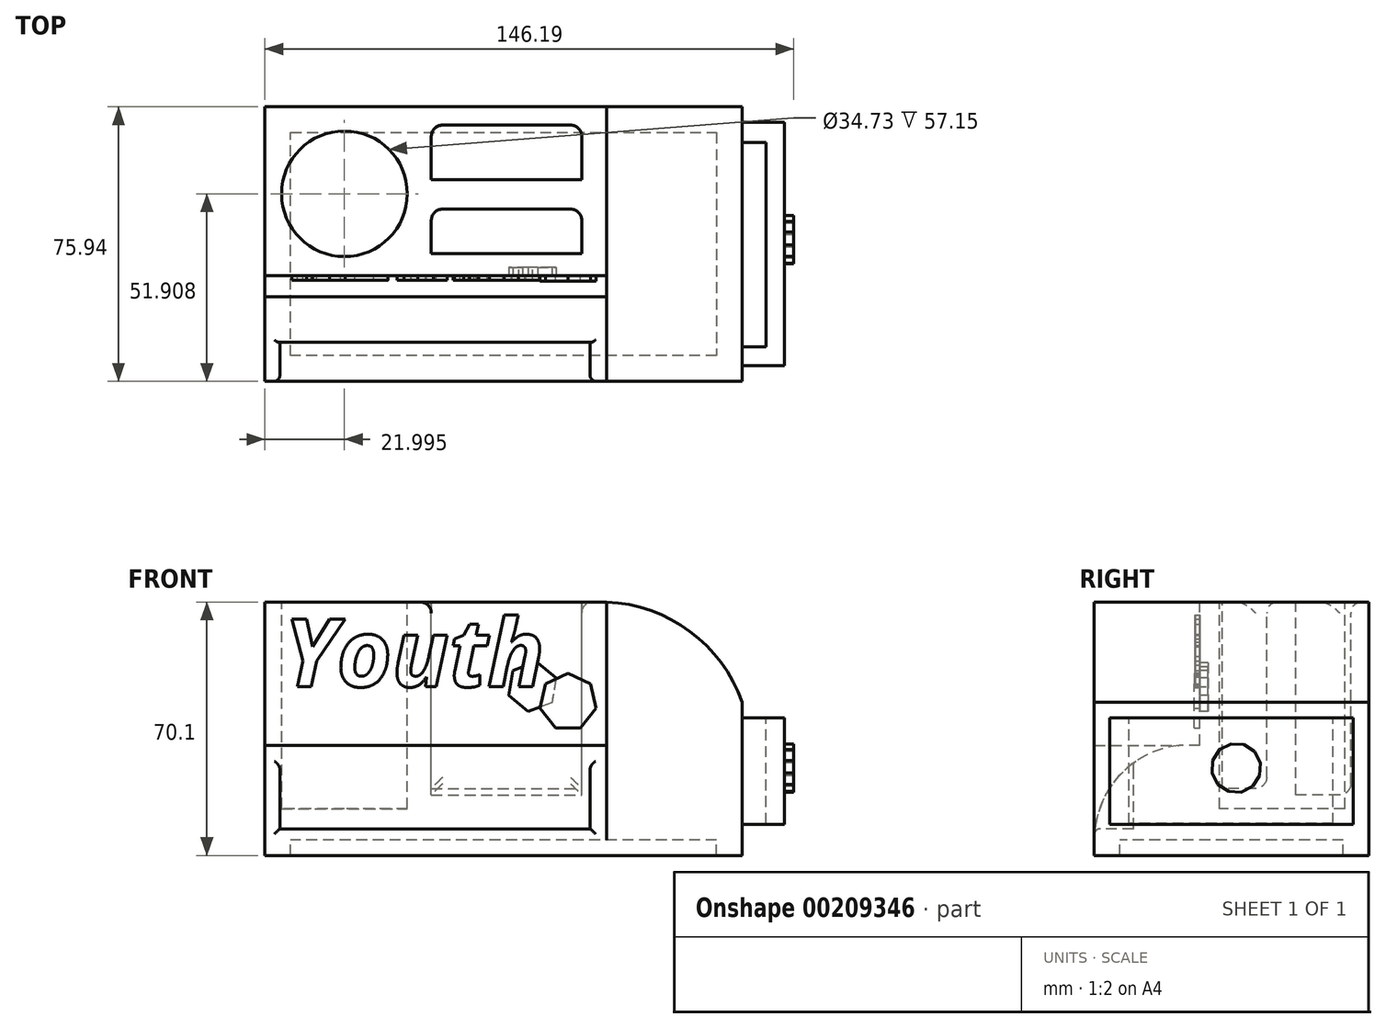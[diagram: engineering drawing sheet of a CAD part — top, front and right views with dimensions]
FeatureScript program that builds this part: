
annotation { "Feature Type Name" : "Feature", "Feature Type Description" : "" }
export const myFeature = defineFeature(function(context is Context, id is Id, definition is map)
    precondition{}
    {
        {
            var Q0;
            Q0=qCreatedBy(makeId("Top.planeOp"),FACE);
            var sketch = newSketch(context, id + "F0", { "sketchPlane" : qUnion([Q0])});
            skLineSegment(sketch, "E0.bottom", {"start": v(-64.17, 27.75) * mm, "end": v(67.8, 27.75) * mm});
            skLineSegment(sketch, "E0.top", {"start": v(-64.17, -38.04) * mm, "end": v(67.8, -38.04) * mm});
            skLineSegment(sketch, "E0.left", {"start": v(-64.17, 27.75) * mm, "end": v(-64.17, -38.04) * mm});
            skLineSegment(sketch, "E0.right", {"start": v(67.8, 27.75) * mm, "end": v(67.8, -38.04) * mm});
            skSolve(sketch);
        }
        {
            var Q0;
            Q0=makeQuery(id+"F0.imprint","IMPRINT",FACE,{"disambiguationData":[TD([[makeQuery(id+"F0.imprint","IMPRINT",EDGE,{"derivedFrom":sQuery(id+"F0.wireOp",EDGE,"E0.bottom")}),-1.0]])]});
            extrude(context, id + "F1", {"entities" : qUnion([Q0]), "depth" : 46.74 * mm});
        }
        {
            var Q0;
            Q0=makeQuery(id+"F1.opExtrude","CAP_FACE",FACE,{"disambiguationData":[OSD([sQuery(id+"F0.wireOp",EDGE,"E0.bottom"),sQuery(id+"F0.wireOp",EDGE,"E0.top"),sQuery(id+"F0.wireOp",EDGE,"E0.left"),sQuery(id+"F0.wireOp",EDGE,"E0.right")])],"isStart":false});
            var sketch = newSketch(context, id + "F2", { "sketchPlane" : qUnion([Q0])});
            skArc(sketch, "E1", {"start": v(-26.64, 27.75) * mm, "mid": v(-49.66, 19.63) * mm, "end": v(-64.17, 0) * mm});
            skSolve(sketch);
        }
        {
            var Q0;
            {var subQ0=sQuery(id+"F2.wireOp",EDGE,"E1");Q0=makeQuery(id+"F2.imprint","IMPRINT",FACE,{"disambiguationData":[TD([[makeQuery(id+"F2.imprint","IMPRINT",EDGE,{"derivedFrom":subQ0}),-1.0]])]});}
            extrude(context, id + "F3", {"entities" : qUnion([Q0]), "operationType" : NewBodyOperationType.REMOVE, "oppositeDirection" : true, "depth" : 47 * mm});
        }
        {
            var Q0;
            Q0=makeQuery(id+"F1.opExtrude","SWEPT_FACE",FACE,{"disambiguationData":[OSD([sQuery(id+"F0.wireOp",EDGE,"E0.bottom")])]});
            var sketch = newSketch(context, id + "F4", { "sketchPlane" : qUnion([Q0])});
            skCircle(sketch, "E2", {"center": v(-45.8, 22.7) * mm, "radius": 17.36 * mm});
            skSolve(sketch);
        }
        {
            var Q0;
            Q0=makeQuery(id+"F4.imprint","IMPRINT",FACE,{"disambiguationData":[TD([[makeQuery(id+"F4.imprint","IMPRINT",EDGE,{"derivedFrom":sQuery(id+"F4.wireOp",EDGE,"E2")}),1.0]])]});
            extrude(context, id + "F5", {"entities" : qUnion([Q0]), "operationType" : NewBodyOperationType.REMOVE, "oppositeDirection" : true, "depth" : 57.15 * mm});
        }
        {
            var Q0;
            Q0=makeQuery(id+"F1.opExtrude","SWEPT_FACE",FACE,{"disambiguationData":[OSD([sQuery(id+"F0.wireOp",EDGE,"E0.bottom")])]});
            var sketch = newSketch(context, id + "F6", { "sketchPlane" : qUnion([Q0])});
            skLineSegment(sketch, "E3.bottom", {"start": v(-21.8, 41.67) * mm, "end": v(19.78, 41.67) * mm});
            skLineSegment(sketch, "E3.top", {"start": v(-21.8, 26.54) * mm, "end": v(19.78, 26.54) * mm});
            skLineSegment(sketch, "E3.left", {"start": v(-21.8, 41.67) * mm, "end": v(-21.8, 26.54) * mm});
            skLineSegment(sketch, "E3.right", {"start": v(19.78, 41.67) * mm, "end": v(19.78, 26.54) * mm});
            skSolve(sketch);
        }
        {
            var Q0;
            Q0=makeQuery(id+"F6.imprint","IMPRINT",FACE,{"disambiguationData":[TD([[makeQuery(id+"F6.imprint","IMPRINT",EDGE,{"derivedFrom":sQuery(id+"F6.wireOp",EDGE,"E3.bottom")}),-1.0]])]});
            extrude(context, id + "F7", {"entities" : qUnion([Q0]), "operationType" : NewBodyOperationType.REMOVE, "oppositeDirection" : true, "depth" : 53.34 * mm});
        }
        {
            var Q0;
            Q0=makeQuery(id+"F1.opExtrude","CAP_FACE",FACE,{"disambiguationData":[OSD([sQuery(id+"F0.wireOp",EDGE,"E0.bottom"),sQuery(id+"F0.wireOp",EDGE,"E0.top"),sQuery(id+"F0.wireOp",EDGE,"E0.left"),sQuery(id+"F0.wireOp",EDGE,"E0.right")])],"isStart":true});
            var sketch = newSketch(context, id + "F8", { "sketchPlane" : qUnion([Q0])});
            skLineSegment(sketch, "E4.bottom", {"start": v(67.8, -27.75) * mm, "end": v(-65.58, -27.75) * mm});
            skLineSegment(sketch, "E4.top", {"start": v(67.8, 38.04) * mm, "end": v(-65.58, 38.04) * mm});
            skLineSegment(sketch, "E4.left", {"start": v(67.8, -27.75) * mm, "end": v(67.8, 38.04) * mm});
            skLineSegment(sketch, "E4.right", {"start": v(-65.58, -27.75) * mm, "end": v(-65.58, 38.04) * mm});
            skSolve(sketch);
        }
        {
            var Q0;
            {var subQ2=sQuery(id+"F8.wireOp",EDGE,"E4.left");Q0=makeQuery(id+"F8.imprint","IMPRINT",FACE,{"disambiguationData":[TD([[makeQuery(id+"F8.imprint","IMPRINT",EDGE,{"derivedFrom":subQ2}),1.0]])]});}
            extrude(context, id + "F9", {"entities" : qUnion([Q0]), "operationType" : NewBodyOperationType.ADD, "depth" : 29.2 * mm});
        }
        {
            var Q0;
            Q0=makeQuery(id+"F9.boolean.opBoolean","MERGE",FACE,{"derivedFrom":[makeQuery(id+"F1.opExtrude","SWEPT_FACE",FACE,{"disambiguationData":[OSD([sQuery(id+"F0.wireOp",EDGE,"E0.bottom")])]}),makeQuery(id+"F9.opExtrude","SWEPT_FACE",FACE,{"disambiguationData":[OSD([sQuery(id+"F8.wireOp",EDGE,"E4.bottom")])]})]});
            var sketch = newSketch(context, id + "F10", { "sketchPlane" : qUnion([Q0])});
            skLineSegment(sketch, "E5.bottom", {"start": v(-67.8, 0) * mm, "end": v(26.64, 0) * mm});
            skLineSegment(sketch, "E5.top", {"start": v(-67.8, -29.21) * mm, "end": v(26.64, -29.21) * mm});
            skLineSegment(sketch, "E5.left", {"start": v(-67.8, 0) * mm, "end": v(-67.8, -29.21) * mm});
            skLineSegment(sketch, "E5.right", {"start": v(26.64, 0) * mm, "end": v(26.64, -29.21) * mm});
            skSolve(sketch);
        }
        {
            var Q0;
            Q0=makeQuery(id+"F10.imprint","IMPRINT",FACE,{"disambiguationData":[TD([[makeQuery(id+"F10.imprint","IMPRINT",EDGE,{"derivedFrom":sQuery(id+"F10.wireOp",EDGE,"E5.bottom")}),-1.0]])]});
            extrude(context, id + "F11", {"entities" : qUnion([Q0]), "operationType" : NewBodyOperationType.REMOVE, "oppositeDirection" : true, "depth" : 39.62 * mm});
        }
        {
            var Q0;
            Q0=makeQuery(id+"F9.boolean.opBoolean","MERGE",FACE,{"derivedFrom":[makeQuery(id+"F1.opExtrude","SWEPT_FACE",FACE,{"disambiguationData":[OSD([sQuery(id+"F0.wireOp",EDGE,"E0.right")])]}),makeQuery(id+"F9.opExtrude","SWEPT_FACE",FACE,{"disambiguationData":[OSD([sQuery(id+"F8.wireOp",EDGE,"E4.left")])]})]});
            var sketch = newSketch(context, id + "F12", { "sketchPlane" : qUnion([Q0])});
            skArc(sketch, "E6", {"start": v(-38.04, -29.21) * mm, "mid": v(-18.43, -20.45) * mm, "end": v(-11.88, 0) * mm});
            skSolve(sketch);
        }
        {
            var Q0;
            {var subQ1=sQuery(id+"F8.wireOp",EDGE,"E4.left");var subQ2=makeQuery(id+"F9.opExtrude","CAP_EDGE",EDGE,{"disambiguationData":[OSD([subQ1])],"isStart":false});Q0=makeQuery(id+"F12.imprint","IMPRINT",FACE,{"disambiguationData":[TD([[makeQuery(id+"F12.imprint","IMPRINT",EDGE,{"derivedFrom":subQ2}),-1.0]])]});}
            extrude(context, id + "F13", {"entities" : qUnion([Q0]), "operationType" : NewBodyOperationType.REMOVE, "oppositeDirection" : true, "depth" : 94.49 * mm});
        }
        {
            var Q0;
            {var subQ0=sQuery(id+"F0.wireOp",EDGE,"E0.left");Q0=makeQuery(id+"F9.boolean.opBoolean","MERGE",FACE,{"derivedFrom":[makeQuery(id+"F1.opExtrude","SWEPT_FACE",FACE,{"disambiguationData":[OSD([subQ0])]}),makeQuery(id+"F9.opExtrude","SWEPT_FACE",FACE,{"disambiguationData":[OSD([subQ0])]})]});}
            var sketch = newSketch(context, id + "F14", { "sketchPlane" : qUnion([Q0])});
            skLineSegment(sketch, "E7.0", {"start": v(4.32, 42.42) * mm, "end": v(4.32, -24.9) * mm});
            skLineSegment(sketch, "E7.1", {"start": v(33.72, 42.42) * mm, "end": v(4.32, 42.42) * mm});
            skLineSegment(sketch, "E7.2", {"start": v(33.72, -24.9) * mm, "end": v(33.72, 42.42) * mm});
            skLineSegment(sketch, "E7.3", {"start": v(4.32, -24.9) * mm, "end": v(33.72, -24.9) * mm});
            skSolve(sketch);
        }
        {
            var Q0;
            Q0=makeQuery(id+"F14.imprint","IMPRINT",FACE,{"disambiguationData":[TD([[makeQuery(id+"F14.imprint","IMPRINT",EDGE,{"derivedFrom":sQuery(id+"F14.wireOp",EDGE,"E7.0")}),1.0]])]});
            extrude(context, id + "F15", {"entities" : qUnion([Q0]), "operationType" : NewBodyOperationType.ADD, "depth" : 11.68 * mm});
        }
        {
            var Q0;
            Q0=makeQuery(id+"F15.opExtrude","SWEPT_FACE",FACE,{"disambiguationData":[OSD([sQuery(id+"F14.wireOp",EDGE,"E7.0")])]});
            var sketch = newSketch(context, id + "F16", { "sketchPlane" : qUnion([Q0])});
            skLineSegment(sketch, "E8.bottom", {"start": v(64.17, 36.83) * mm, "end": v(70.67, 36.83) * mm});
            skLineSegment(sketch, "E8.top", {"start": v(64.17, -19.67) * mm, "end": v(70.67, -19.67) * mm});
            skLineSegment(sketch, "E8.left", {"start": v(64.17, 36.83) * mm, "end": v(64.17, -19.67) * mm});
            skLineSegment(sketch, "E8.right", {"start": v(70.67, 36.83) * mm, "end": v(70.67, -19.67) * mm});
            skSolve(sketch);
        }
        {
            var Q0;
            Q0=makeQuery(id+"F16.imprint","IMPRINT",FACE,{"disambiguationData":[TD([[makeQuery(id+"F16.imprint","IMPRINT",EDGE,{"derivedFrom":sQuery(id+"F16.wireOp",EDGE,"E8.bottom")}),-1.0]])]});
            extrude(context, id + "F17", {"entities" : qUnion([Q0]), "operationType" : NewBodyOperationType.REMOVE, "oppositeDirection" : true, "depth" : 29.2 * mm});
        }
        {
            var Q0;
            Q0=makeQuery(id+"F15.opExtrude","CAP_FACE",FACE,{"disambiguationData":[OSD([sQuery(id+"F14.wireOp",EDGE,"E7.0"),sQuery(id+"F14.wireOp",EDGE,"E7.1"),sQuery(id+"F14.wireOp",EDGE,"E7.2"),sQuery(id+"F14.wireOp",EDGE,"E7.3")])],"isStart":false});
            var sketch = newSketch(context, id + "F18", { "sketchPlane" : qUnion([Q0])});
            skCircle(sketch, "E9.cCircle", {"center": v(18.16, 9.99) * mm, "radius": 6.8 * mm, "construction": true});
            skLineSegment(sketch, "E9.0", {"start": v(19.57, 3.33) * mm, "end": v(16.05, 3.52) * mm});
            skLineSegment(sketch, "E9.1", {"start": v(16.05, 3.52) * mm, "end": v(13.1, 5.44) * mm});
            skLineSegment(sketch, "E9.2", {"start": v(13.1, 5.44) * mm, "end": v(11.5, 8.58) * mm});
            skLineSegment(sketch, "E9.3", {"start": v(11.5, 8.58) * mm, "end": v(11.69, 12.1) * mm});
            skLineSegment(sketch, "E9.4", {"start": v(11.69, 12.1) * mm, "end": v(13.6, 15.05) * mm});
            skLineSegment(sketch, "E9.5", {"start": v(13.6, 15.05) * mm, "end": v(16.75, 16.65) * mm});
            skLineSegment(sketch, "E9.6", {"start": v(16.75, 16.65) * mm, "end": v(20.27, 16.46) * mm});
            skLineSegment(sketch, "E9.7", {"start": v(20.27, 16.46) * mm, "end": v(23.22, 14.54) * mm});
            skLineSegment(sketch, "E9.8", {"start": v(23.22, 14.54) * mm, "end": v(24.82, 11.4) * mm});
            skLineSegment(sketch, "E9.9", {"start": v(24.82, 11.4) * mm, "end": v(24.63, 7.88) * mm});
            skLineSegment(sketch, "E9.10", {"start": v(24.63, 7.88) * mm, "end": v(22.71, 4.93) * mm});
            skLineSegment(sketch, "E9.11", {"start": v(22.71, 4.93) * mm, "end": v(19.57, 3.33) * mm});
            skSolve(sketch);
        }
        {
            var Q0;
            Q0=makeQuery(id+"F18.imprint","IMPRINT",FACE,{"disambiguationData":[TD([[makeQuery(id+"F18.imprint","IMPRINT",EDGE,{"derivedFrom":sQuery(id+"F18.wireOp",EDGE,"E9.0")}),-1.0]])]});
            extrude(context, id + "F19", {"entities" : qUnion([Q0]), "operationType" : NewBodyOperationType.ADD, "depth" : 2.54 * mm});
        }
        {
            var Q0;
            Q0=makeQuery(id+"F9.boolean.opBoolean","MERGE",FACE,{"derivedFrom":[makeQuery(id+"F1.opExtrude","SWEPT_FACE",FACE,{"disambiguationData":[OSD([sQuery(id+"F0.wireOp",EDGE,"E0.top")])]}),makeQuery(id+"F9.opExtrude","SWEPT_FACE",FACE,{"disambiguationData":[OSD([sQuery(id+"F8.wireOp",EDGE,"E4.top")])]})]});
            var sketch = newSketch(context, id + "F20", { "sketchPlane" : qUnion([Q0])});
            skLineSegment(sketch, "E10.0", {"start": v(-57.06, -22.1) * mm, "end": v(-26.69, -22.1) * mm});
            skLineSegment(sketch, "E10.1", {"start": v(-57.06, 39.62) * mm, "end": v(-57.06, -22.1) * mm});
            skLineSegment(sketch, "E10.2", {"start": v(-26.69, -22.1) * mm, "end": v(60.69, -22.1) * mm});
            skLineSegment(sketch, "E10.3", {"start": v(60.69, -22.1) * mm, "end": v(60.69, 39.62) * mm});
            skLineSegment(sketch, "E10.4", {"start": v(60.69, 39.62) * mm, "end": v(-57.06, 39.62) * mm});
            skSolve(sketch);
        }
        {
            var Q0;
            Q0=makeQuery(id+"F20.imprint","IMPRINT",FACE,{"disambiguationData":[TD([[makeQuery(id+"F20.imprint","IMPRINT",EDGE,{"derivedFrom":sQuery(id+"F20.wireOp",EDGE,"E10.0")}),-1.0]])]});
            extrude(context, id + "F21", {"entities" : qUnion([Q0]), "operationType" : NewBodyOperationType.ADD, "depth" : 4.32 * mm});
        }
        {
            var Q0;
            Q0=makeQuery(id+"F1.opExtrude","SWEPT_BODY",BODY,{"disambiguationData":[OSD([sQuery(id+"F0.wireOp",EDGE,"E0.bottom"),sQuery(id+"F0.wireOp",EDGE,"E0.top"),sQuery(id+"F0.wireOp",EDGE,"E0.left"),sQuery(id+"F0.wireOp",EDGE,"E0.right")])]});
            var Q1;
            Q1=makeQuery(id+"F21.opExtrude","CAP_EDGE",EDGE,{"disambiguationData":[OSD([sQuery(id+"F0.wireOp",EDGE,"E0.top")])],"isStart":false});
            transform(context, id + "F22", {"entities" : qUnion([Q0]), "transformType" : TransformType.ROTATION, "transformAxis" : qUnion([Q1]), "angle" : 90 * degree, "makeCopy" : false});
        }
        {
            var Q0;
            Q0=makeQuery(id+"F1.opExtrude","SWEPT_BODY",BODY,{"disambiguationData":[OSD([sQuery(id+"F0.wireOp",EDGE,"E0.bottom"),sQuery(id+"F0.wireOp",EDGE,"E0.top"),sQuery(id+"F0.wireOp",EDGE,"E0.left"),sQuery(id+"F0.wireOp",EDGE,"E0.right")])]});
            var Q1;
            Q1=makeQuery(id+"F21.opExtrude","CAP_EDGE",EDGE,{"disambiguationData":[OSD([sQuery(id+"F0.wireOp",EDGE,"E0.top"),sQuery(id+"F0.wireOp",EDGE,"E0.right"),sQuery(id+"F8.wireOp",EDGE,"E4.top"),sQuery(id+"F8.wireOp",EDGE,"E4.left")])],"isStart":false});
            transform(context, id + "F23", {"entities" : qUnion([Q0]), "transformType" : TransformType.ROTATION, "transformAxis" : qUnion([Q1]), "angle" : 180 * degree, "oppositeDirection" : true, "makeCopy" : false});
        }
        {
            var Q0;
            Q0=makeQuery(id+"F1.opExtrude","SWEPT_BODY",BODY,{"disambiguationData":[OSD([sQuery(id+"F0.wireOp",EDGE,"E0.bottom"),sQuery(id+"F0.wireOp",EDGE,"E0.top"),sQuery(id+"F0.wireOp",EDGE,"E0.left"),sQuery(id+"F0.wireOp",EDGE,"E0.right")])]});
            var Q1;
            Q1=makeQuery(id+"F1.opExtrude","CAP_EDGE",EDGE,{"disambiguationData":[OSD([sQuery(id+"F0.wireOp",EDGE,"E0.bottom")])],"isStart":false});
            transform(context, id + "F24", {"entities" : qUnion([Q0]), "transformType" : TransformType.ROTATION, "transformAxis" : qUnion([Q1]), "angle" : 180 * degree, "oppositeDirection" : true, "makeCopy" : false});
        }
        {
            var Q0;
            Q0=makeQuery(id+"F1.opExtrude","SWEPT_BODY",BODY,{"disambiguationData":[OSD([sQuery(id+"F0.wireOp",EDGE,"E0.bottom"),sQuery(id+"F0.wireOp",EDGE,"E0.top"),sQuery(id+"F0.wireOp",EDGE,"E0.left"),sQuery(id+"F0.wireOp",EDGE,"E0.right")])]});
            var Q1;
            Q1=makeQuery(id+"F21.opExtrude","CAP_EDGE",EDGE,{"disambiguationData":[OSD([sQuery(id+"F0.wireOp",EDGE,"E0.top"),sQuery(id+"F0.wireOp",EDGE,"E0.right"),sQuery(id+"F8.wireOp",EDGE,"E4.top"),sQuery(id+"F8.wireOp",EDGE,"E4.left"),sQuery(id+"F12.wireOp",EDGE,"E6")])],"isStart":false});
            transform(context, id + "F25", {"entities" : qUnion([Q0]), "transformType" : TransformType.TRANSLATION_DISTANCE, "transformDirection" : qUnion([Q1]), "distance" : 157.48 * mm, "makeCopy" : false});
        }
        {
            var Q0;
            Q0=makeQuery(id+"F1.opExtrude","SWEPT_BODY",BODY,{"disambiguationData":[OSD([sQuery(id+"F0.wireOp",EDGE,"E0.bottom"),sQuery(id+"F0.wireOp",EDGE,"E0.top"),sQuery(id+"F0.wireOp",EDGE,"E0.left"),sQuery(id+"F0.wireOp",EDGE,"E0.right")])]});
            var Q1;
            Q1=makeQuery(id+"F1.opExtrude","CAP_EDGE",EDGE,{"disambiguationData":[OSD([sQuery(id+"F0.wireOp",EDGE,"E0.bottom")])],"isStart":false});
            transform(context, id + "F26", {"entities" : qUnion([Q0]), "transformType" : TransformType.TRANSLATION_DISTANCE, "transformDirection" : qUnion([Q1]), "distance" : 19.56 * mm, "oppositeDirection" : true, "makeCopy" : false});
        }
        {
            var Q0;
            Q0=makeQuery(id+"F1.opExtrude","SWEPT_BODY",BODY,{"disambiguationData":[OSD([sQuery(id+"F0.wireOp",EDGE,"E0.bottom"),sQuery(id+"F0.wireOp",EDGE,"E0.top"),sQuery(id+"F0.wireOp",EDGE,"E0.left"),sQuery(id+"F0.wireOp",EDGE,"E0.right")])]});
            var Q1;
            {var subQ0=sQuery(id+"F0.wireOp",EDGE,"E0.right");Q1=makeQuery(id+"F21.boolean.opBoolean","MERGE",EDGE,{"derivedFrom":[makeQuery(id+"F1.opExtrude","CAP_EDGE",EDGE,{"disambiguationData":[OSD([subQ0])],"isStart":false}),makeQuery(id+"F21.opExtrude","SWEPT_EDGE",EDGE,{"disambiguationData":[OSD([sQuery(id+"F0.wireOp",EDGE,"E0.top"),subQ0,sQuery(id+"F8.wireOp",EDGE,"E4.top"),sQuery(id+"F8.wireOp",EDGE,"E4.left")])]})]});}
            transform(context, id + "F27", {"entities" : qUnion([Q0]), "transformType" : TransformType.TRANSLATION_DISTANCE, "transformDirection" : qUnion([Q1]), "distance" : 58.17 * mm, "oppositeDirection" : true, "makeCopy" : false});
        }
        {
            var Q0;
            Q0=makeQuery(id+"F1.opExtrude","SWEPT_BODY",BODY,{"disambiguationData":[OSD([sQuery(id+"F0.wireOp",EDGE,"E0.bottom"),sQuery(id+"F0.wireOp",EDGE,"E0.top"),sQuery(id+"F0.wireOp",EDGE,"E0.left"),sQuery(id+"F0.wireOp",EDGE,"E0.right")])]});
            var Q1;
            Q1=makeQuery(id+"F21.opExtrude","CAP_EDGE",EDGE,{"disambiguationData":[OSD([sQuery(id+"F0.wireOp",EDGE,"E0.top"),sQuery(id+"F0.wireOp",EDGE,"E0.left"),sQuery(id+"F8.wireOp",EDGE,"E4.top")])],"isStart":false});
            transform(context, id + "F28", {"entities" : qUnion([Q0]), "transformType" : TransformType.TRANSLATION_DISTANCE, "transformDirection" : qUnion([Q1]), "distance" : 80.52 * mm, "oppositeDirection" : true, "makeCopy" : false});
        }
        {
            var Q0;
            Q0=makeQuery(id+"F11.boolean.opBoolean","COPY",FACE,{"derivedFrom":makeQuery(id+"F11.opExtrude","SWEPT_FACE",FACE,{"disambiguationData":[OSD([sQuery(id+"F10.wireOp",EDGE,"E5.bottom")])]})});
            var sketch = newSketch(context, id + "F29", { "sketchPlane" : qUnion([Q0])});
            skText(sketch, "E11", { "text": "Youth", "fontName": "OpenSans-BoldItalic.ttf"});
            const initialGuessF29  = {"E11": [-0.06498, 0.0114, 1, 0, 0.01877]};
            skSetInitialGuess(sketch, initialGuessF29);
            skSolve(sketch);
        }
        {
            var Q0;
            Q0 = qSketchRegion(id + "F29", true);
            extrude(context, id + "F30", {"entities" : qUnion([Q0]), "operationType" : NewBodyOperationType.ADD, "depth" : 1.27 * mm});
        }
        {
            var Q0;
            Q0=makeQuery(id+"F9.boolean.opBoolean","MERGE",FACE,{"derivedFrom":[makeQuery(id+"F1.opExtrude","SWEPT_FACE",FACE,{"disambiguationData":[OSD([sQuery(id+"F0.wireOp",EDGE,"E0.bottom")])]}),makeQuery(id+"F9.opExtrude","SWEPT_FACE",FACE,{"disambiguationData":[OSD([sQuery(id+"F8.wireOp",EDGE,"E4.bottom")])]})]});
            var sketch = newSketch(context, id + "F31", { "sketchPlane" : qUnion([Q0])});
            skLineSegment(sketch, "E12.bottom", {"start": v(-24.11, 9.86) * mm, "end": v(17.46, 9.86) * mm});
            skLineSegment(sketch, "E12.top", {"start": v(-24.11, -2.41) * mm, "end": v(17.46, -2.41) * mm});
            skLineSegment(sketch, "E12.left", {"start": v(-24.11, 9.86) * mm, "end": v(-24.11, -2.41) * mm});
            skLineSegment(sketch, "E12.right", {"start": v(17.46, 9.86) * mm, "end": v(17.46, -2.41) * mm});
            skSolve(sketch);
        }
        {
            var Q0;
            Q0=makeQuery(id+"F31.imprint","IMPRINT",FACE,{"disambiguationData":[TD([[makeQuery(id+"F31.imprint","IMPRINT",EDGE,{"derivedFrom":sQuery(id+"F31.wireOp",EDGE,"E12.bottom")}),-1.0]])]});
            extrude(context, id + "F32", {"entities" : qUnion([Q0]), "operationType" : NewBodyOperationType.REMOVE, "oppositeDirection" : true, "depth" : 51.56 * mm});
        }
        {
            var Q0;
            Q0=makeQuery(id+"F32.boolean.opBoolean","COPY",FACE,{"derivedFrom":makeQuery(id+"F32.opExtrude","SWEPT_FACE",FACE,{"disambiguationData":[OSD([sQuery(id+"F31.wireOp",EDGE,"E12.bottom")])]})});
            fillet(context, id + "F33", {"entities" : qUnion([Q0]), "radius" : 3.07 * mm, "tangentPropagation" : true, "allowEdgeOverflow" : false});
        }
        {
            var Q0;
            Q0=makeQuery(id+"F7.boolean.opBoolean","COPY",EDGE,{"derivedFrom":makeQuery(id+"F7.opExtrude","CAP_EDGE",EDGE,{"disambiguationData":[OSD([sQuery(id+"F6.wireOp",EDGE,"E3.left")])],"isStart":true})});
            var Q1;
            Q1=makeQuery(id+"F7.boolean.opBoolean","COPY",EDGE,{"derivedFrom":makeQuery(id+"F7.opExtrude","CAP_EDGE",EDGE,{"disambiguationData":[OSD([sQuery(id+"F6.wireOp",EDGE,"E3.bottom")])],"isStart":true})});
            var Q2;
            Q2=makeQuery(id+"F7.boolean.opBoolean","COPY",EDGE,{"derivedFrom":makeQuery(id+"F7.opExtrude","CAP_EDGE",EDGE,{"disambiguationData":[OSD([sQuery(id+"F6.wireOp",EDGE,"E3.right")])],"isStart":true})});
            var Q3;
            Q3=makeQuery(id+"F7.boolean.opBoolean","COPY",FACE,{"derivedFrom":makeQuery(id+"F7.opExtrude","SWEPT_FACE",FACE,{"disambiguationData":[OSD([sQuery(id+"F6.wireOp",EDGE,"E3.bottom")])]})});
            fillet(context, id + "F34", {"entities" : qUnion([Q0, Q1, Q2, Q3]), "radius" : 3.07 * mm, "tangentPropagation" : true, "allowEdgeOverflow" : false});
        }
        {
            var Q0;
            {var subQ5=sQuery(id+"F0.wireOp",EDGE,"E0.bottom");var subQ6=sQuery(id+"F10.wireOp",EDGE,"E5.bottom");Q0=makeQuery(id+"F30.boolean.opBoolean","SPLIT",FACE,{"disambiguationData":[TD([makeQuery(id+"F1.opExtrude","SWEPT_FACE",FACE,{"disambiguationData":[OSD([subQ5])]})])],"derivedFrom":makeQuery(id+"F11.boolean.opBoolean","COPY",FACE,{"derivedFrom":makeQuery(id+"F11.opExtrude","SWEPT_FACE",FACE,{"disambiguationData":[OSD([subQ6])]})})});}
            var sketch = newSketch(context, id + "F35", { "sketchPlane" : qUnion([Q0])});
            skCircle(sketch, "E13.cCircle", {"center": v(3.84, 11.4) * mm, "radius": 6.02 * mm, "construction": true});
            skLineSegment(sketch, "E13.0", {"start": v(2.68, 4.54) * mm, "end": v(-2.68, 8.98) * mm});
            skLineSegment(sketch, "E13.1", {"start": v(-2.68, 8.98) * mm, "end": v(-1.52, 15.83) * mm});
            skLineSegment(sketch, "E13.2", {"start": v(-1.52, 15.83) * mm, "end": v(5, 18.26) * mm});
            skLineSegment(sketch, "E13.3", {"start": v(5, 18.26) * mm, "end": v(10.36, 13.83) * mm});
            skLineSegment(sketch, "E13.4", {"start": v(10.36, 13.83) * mm, "end": v(9.2, 6.97) * mm});
            skLineSegment(sketch, "E13.5", {"start": v(9.2, 6.97) * mm, "end": v(2.68, 4.54) * mm});
            skPoint(sketch, "E13.0.midPoint", {"position": v(0, 6.76) * mm});
            skSolve(sketch);
        }
        {
            var Q0;
            Q0=makeQuery(id+"F35.imprint","IMPRINT",FACE,{"disambiguationData":[TD([[makeQuery(id+"F35.imprint","IMPRINT",EDGE,{"derivedFrom":sQuery(id+"F35.wireOp",EDGE,"E13.0")}),1.0]])]});
            var sketch = newSketch(context, id + "F36", { "sketchPlane" : qUnion([Q0])});
            skCircle(sketch, "E14.cCircle", {"center": v(13.67, 7.16) * mm, "radius": 7.16 * mm, "construction": true});
            skLineSegment(sketch, "E14.0", {"start": v(17.12, 0) * mm, "end": v(10.22, 0) * mm});
            skLineSegment(sketch, "E14.1", {"start": v(10.22, 0) * mm, "end": v(5.92, 5.4) * mm});
            skLineSegment(sketch, "E14.2", {"start": v(5.92, 5.4) * mm, "end": v(7.46, 12.12) * mm});
            skLineSegment(sketch, "E14.3", {"start": v(7.46, 12.12) * mm, "end": v(13.67, 15.11) * mm});
            skLineSegment(sketch, "E14.4", {"start": v(13.67, 15.11) * mm, "end": v(19.89, 12.12) * mm});
            skLineSegment(sketch, "E14.5", {"start": v(19.89, 12.12) * mm, "end": v(21.42, 5.4) * mm});
            skLineSegment(sketch, "E14.6", {"start": v(21.42, 5.4) * mm, "end": v(17.12, 0) * mm});
            skPoint(sketch, "E14.0.midPoint", {"position": v(13.67, 0) * mm});
            skSolve(sketch);
        }
        {
            var Q0;
            Q0=makeQuery(id+"F35.imprint","IMPRINT",FACE,{"disambiguationData":[TD([[makeQuery(id+"F35.imprint","IMPRINT",EDGE,{"derivedFrom":sQuery(id+"F35.wireOp",EDGE,"E13.0")}),-1.0]])]});
            extrude(context, id + "F37", {"entities" : qUnion([Q0]), "operationType" : NewBodyOperationType.REMOVE, "oppositeDirection" : true, "depth" : 2.3 * mm});
        }
        {
            var Q0;
            Q0=makeQuery(id+"F36.imprint","IMPRINT",FACE,{"disambiguationData":[TD([[makeQuery(id+"F36.imprint","IMPRINT",EDGE,{"derivedFrom":sQuery(id+"F36.wireOp",EDGE,"E14.0")}),-1.0]])]});
            var Q1;
            {var subQ0=sQuery(id+"F36.wireOp",EDGE,"E14.3");var subQ1=sQuery(id+"F36.wireOp",EDGE,"E14.2");var subQ2=makeQuery(id+"F36.imprint","INTERSECT",VERTEX,{"derivedFrom":[subQ1,subQ0]});Q1=makeQuery(id+"F36.imprint","IMPRINT",FACE,{"disambiguationData":[TD([[makeQuery(id+"F36.imprint","IMPRINT",EDGE,{"disambiguationData":[TD([[subQ2,1.0]])],"derivedFrom":subQ1}),-1.0]])]});}
            extrude(context, id + "F38", {"entities" : qUnion([Q0, Q1]), "operationType" : NewBodyOperationType.ADD, "depth" : 1.52 * mm});
        }
        {
            var Q0;
            Q0=qCreatedBy(makeId("Top.planeOp"),FACE);
            var sketch = newSketch(context, id + "F39", { "sketchPlane" : qUnion([Q0])});
            skLineSegment(sketch, "E15.bottom", {"start": v(-65.99, -26.97) * mm, "end": v(19.78, -26.97) * mm});
            skLineSegment(sketch, "E15.top", {"start": v(-65.99, -60.64) * mm, "end": v(19.78, -60.64) * mm});
            skLineSegment(sketch, "E15.left", {"start": v(-65.99, -26.97) * mm, "end": v(-65.99, -60.64) * mm});
            skLineSegment(sketch, "E15.right", {"start": v(19.78, -26.97) * mm, "end": v(19.78, -60.64) * mm});
            skSolve(sketch);
        }
        {
            var Q0;
            Q0=makeQuery(id+"F39.imprint","IMPRINT",FACE,{"disambiguationData":[TD([[makeQuery(id+"F39.imprint","IMPRINT",EDGE,{"derivedFrom":sQuery(id+"F39.wireOp",EDGE,"E15.bottom")}),-1.0]])]});
            extrude(context, id + "F40", {"entities" : qUnion([Q0]), "operationType" : NewBodyOperationType.REMOVE, "oppositeDirection" : true, "depth" : 27.94 * mm});
        }
        {
            var Q0;
            Q0=makeQuery(id+"F40.boolean.opBoolean","INTERSECT",EDGE,{"derivedFrom":[makeQuery(id+"F13.boolean.opBoolean","COPY",FACE,{"derivedFrom":makeQuery(id+"F13.opExtrude","SWEPT_FACE",FACE,{"disambiguationData":[OSD([sQuery(id+"F12.wireOp",EDGE,"E6")])]})}),makeQuery(id+"F40.opExtrude","SWEPT_FACE",FACE,{"disambiguationData":[OSD([sQuery(id+"F39.wireOp",EDGE,"E15.bottom")])]})]});
            var Q1;
            Q1=makeQuery(id+"F40.boolean.opBoolean","INTERSECT",EDGE,{"derivedFrom":[makeQuery(id+"F13.boolean.opBoolean","COPY",FACE,{"derivedFrom":makeQuery(id+"F13.opExtrude","SWEPT_FACE",FACE,{"disambiguationData":[OSD([sQuery(id+"F12.wireOp",EDGE,"E6")])]})}),makeQuery(id+"F40.opExtrude","SWEPT_FACE",FACE,{"disambiguationData":[OSD([sQuery(id+"F39.wireOp",EDGE,"E15.left")])]})]});
            var Q2;
            Q2=makeQuery(id+"F40.boolean.opBoolean","INTERSECT",EDGE,{"derivedFrom":[makeQuery(id+"F13.boolean.opBoolean","COPY",FACE,{"derivedFrom":makeQuery(id+"F13.opExtrude","SWEPT_FACE",FACE,{"disambiguationData":[OSD([sQuery(id+"F12.wireOp",EDGE,"E6")])]})}),makeQuery(id+"F40.opExtrude","SWEPT_FACE",FACE,{"disambiguationData":[OSD([sQuery(id+"F39.wireOp",EDGE,"E15.right")])]})]});
            var Q3;
            Q3=makeQuery(id+"F40.boolean.opBoolean","INTERSECT",EDGE,{"derivedFrom":[makeQuery(id+"F13.boolean.opBoolean","COPY",FACE,{"derivedFrom":makeQuery(id+"F13.opExtrude","SWEPT_FACE",FACE,{"disambiguationData":[OSD([sQuery(id+"F12.wireOp",EDGE,"E6")])]})}),makeQuery(id+"F40.opExtrude","CAP_FACE",FACE,{"disambiguationData":[OSD([sQuery(id+"F39.wireOp",EDGE,"E15.bottom"),sQuery(id+"F39.wireOp",EDGE,"E15.top"),sQuery(id+"F39.wireOp",EDGE,"E15.left"),sQuery(id+"F39.wireOp",EDGE,"E15.right")])],"isStart":false})]});
            fillet(context, id + "F41", {"entities" : qUnion([Q0, Q1, Q2, Q3]), "radius" : 1.5 * mm, "tangentPropagation" : true, "allowEdgeOverflow" : false});
        }
    });
